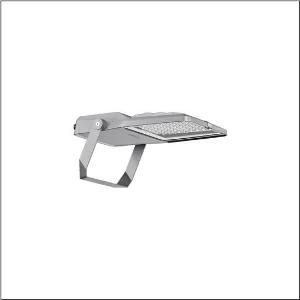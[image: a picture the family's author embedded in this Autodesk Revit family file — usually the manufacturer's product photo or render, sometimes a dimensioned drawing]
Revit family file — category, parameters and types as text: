
# Revit family: floodlight_fl_21_iq_mini___pl43_5xa7771d2a1a_9b6a
name_source: partatom
category: Lighting Fixtures
units: mm (PartAtom-declared; Revit-internal decimal feet)

## family parameters
Cut with Voids When Loaded = No
Host = Face
Light Source = No
Part Type = Normal
Room Calculation Point = No
Round Connector Dimension = Use Diameter
Shared = No

## types (1)
- --- (1 x LED, 18290 lm, 143 W, 3000K)
    Apparent Load = 143 VA
    CIE Flux Codes = 27 78 99 100 100
    Color Rendering = 70
    Color Temperature = 3000K
    Default Elevation = 1800 mm
    Description = Floodlight FL 21 iQ mini, floodlight, primary light control with lens, of PMMA, primary optical cover: protective disc, of toughened safety glass, transparent, light distribution: PL43, light emission: direct distribution, installation type: surface-mounted, lamps: LED, High Power LED, rated values: 18.290lm | 143W | 127,9lm/W (begin service life); end service life: 18.290lm | 151,6W; at 50% lumin. flux: 9.145lm | 60,6W | 150,9lm/W, colour temperature: 3000K, colour rendering: CRI > 70, light colour: 730, light setting 1 begin service life: 100% | 18.290lm | 143W | 127,9lm/W | 3.000K, light setting 1 end service life: 151,6W, further light settings possible, control: Auto-Match, Temp-Guard, Lumen-Switch, Night-Set, Smart-Wire, Light-Fading, Desk-Remote (wireless, voltage-free reading and setting of iQ features in the workshop via application-optimized NFC function/RFID function), optimised constant luminous flux control (CLO 2.0), pre-setting: linear dimming characteristic, with terminal, 6-pole, mains connection: 220..240V, AC, 50/60Hz, luminaire housing, of diecast aluminium, powder-coated, SITECO metallic grey (DB 702S), corrosivity category C5 mid according to DIN EN ISO 12944suitable for swimming poolschlorine-resistant, sealing non-destructively replaceable, mounting bracket, of steel, galvanised, powder-coated, SITECO metallic grey (DB 702S), protection rating (complete): IP66, insulation class (complete): insulation class II (safety insulation), certification: CE, ENEC, VDE, protection symbol: D, impact resistance: IK08, permissible operating ambient temperature: -40..+40°C, permissible operating ambient temperature for outdoor applications: -40..+50°C, standard: DIN EN 12944, LABS conformity tested according to VDMA 24364:2018-05, packaging unit: 1 piece

Light Distribution: PL43
    Height = 70 mm
    Lamp = 1 x LED
    Lamp Light Flux = 18290 lm
    Lamp Power = 143 W
    Lamp count = 1
    Length = 485 mm
    Luminous efficacy = 128 lm/W
    Manufacturer = Siteco
    ModVariant = No
    Model = 5XA7771D2A1A
    Mounting Place = Pole
    Mounting Type = Pole annexe
    Number of Poles = 1
    OnlyDefault = Yes
    Power Factor = 1
    Product Name = Floodlight FL 21 iQ mini | PL43
    Product group = floodlight | pylon annexe
    ProductGroupID = 6201
    Protection Class = Protection class II
    Protection Degree = IP 66
    RLX_Detail_Level = 1
    RLX_Emergency_Light_Flux = 0 lm
    RLX_Emergency_Type = 0
    RLX_Emergency_Type_DB = No
    RlxData = <blob elided: 96653 chars, md5=1f570041>
    Socket = socket
    Standby Power = 0 W
    System Light Flux = 18290 lm
    System Power = 143 W
    Type Comments = factory setting: luminous flux: 100 % | dim-lin: 254 | 730 mA
    Type Image = l_1006845.jpg
    URL = http://relux.com
    VarID = @adj_163105
    Voltage = 0 V
    Weight = 0.00 kg
    Width = 337 mm

## geometry (parser evidence)
native form markers: Blend x4, Sweep x12
no freeform markers — native parametric forms only
